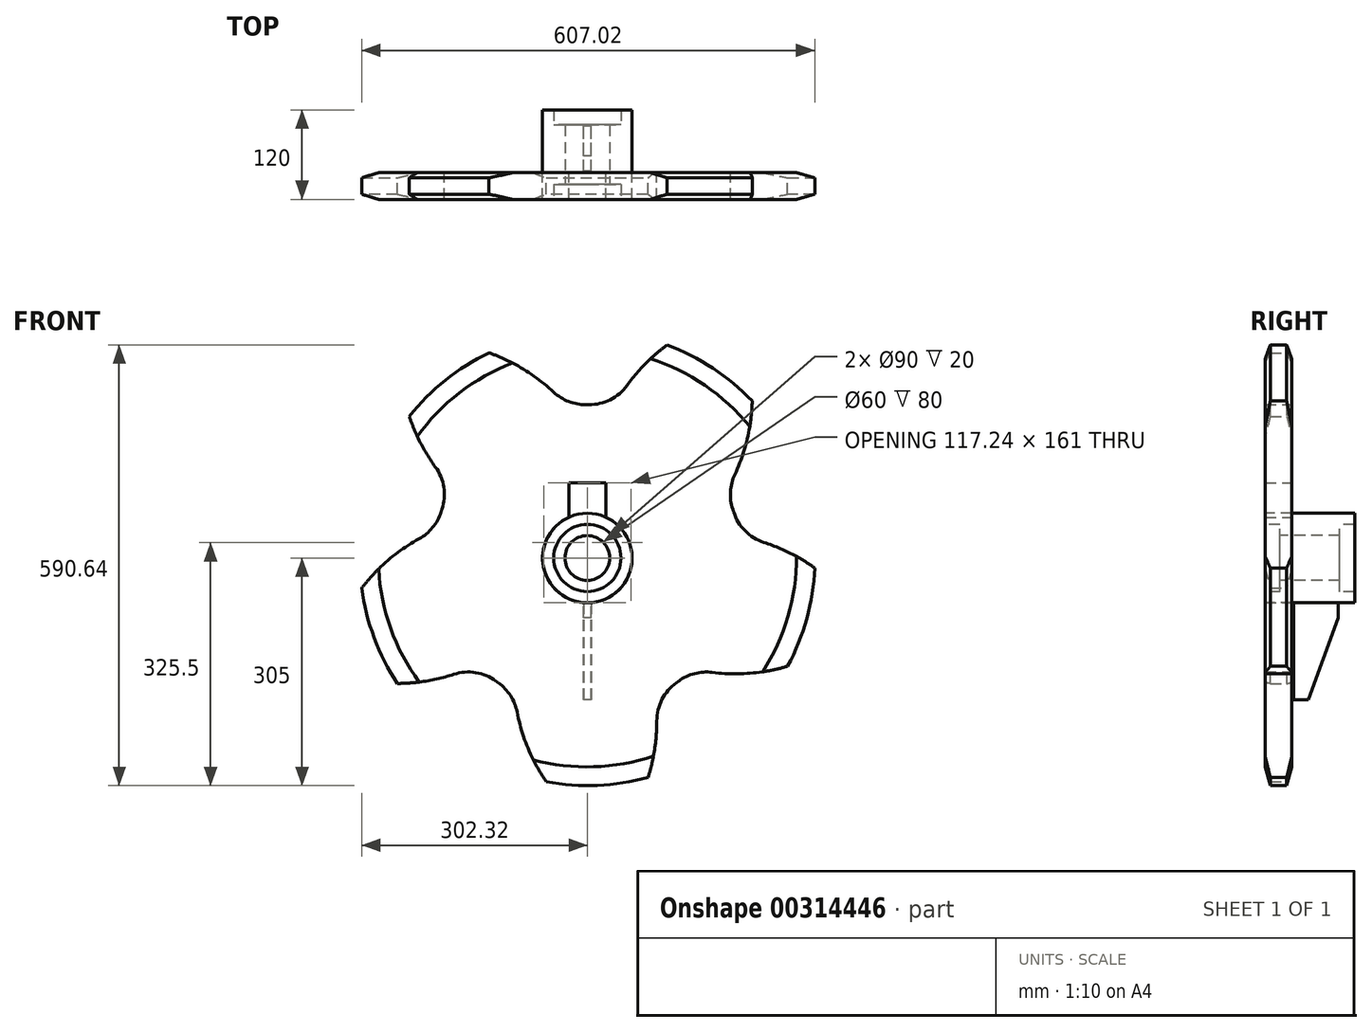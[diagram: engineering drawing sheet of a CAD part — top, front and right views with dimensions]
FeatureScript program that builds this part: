
annotation { "Feature Type Name" : "Feature", "Feature Type Description" : "" }
export const myFeature = defineFeature(function(context is Context, id is Id, definition is map)
    precondition{}
    {
        {
            var Q0;
            Q0=qCreatedBy(makeId("Front.planeOp"),FACE);
            var sketch = newSketch(context, id + "F0", { "sketchPlane" : qUnion([Q0])});
            skArc(sketch, "E0.0", {"start": v(-131.78, 275.06) * mm, "mid": v(-190.02, 238.57) * mm, "end": v(-238.6, 189.98) * mm});
            skLineSegment(sketch, "E1", {"start": v(-25, 54.54) * mm, "end": v(-25, 101) * mm});
            skLineSegment(sketch, "E2", {"start": v(-25, 101) * mm, "end": v(25, 101) * mm});
            skLineSegment(sketch, "E3", {"start": v(25, 101) * mm, "end": v(25, 54.54) * mm});
            skLineSegment(sketch, "E4", {"start": v(0, 0) * mm, "end": v(0, 397.7) * mm, "construction": true});
            skArc(sketch, "E5", {"start": v(25, 54.54) * mm, "mid": v(0, 60) * mm, "end": v(-25, 54.54) * mm, "construction": true});
            skArc(sketch, "E6", {"start": v(-25, 54.54) * mm, "mid": v(0, -60) * mm, "end": v(25, 54.54) * mm});
            skCircle(sketch, "E7", {"center": v(0, 0) * mm, "radius": 268 * mm, "construction": true});
            skCircle(sketch, "E8", {"center": v(0, 0) * mm, "radius": 218.5 * mm, "construction": true});
            skLineSegment(sketch, "E9", {"start": v(2.5, 288.37) * mm, "end": v(2.5, 267.99) * mm, "construction": true});
            skLineSegment(sketch, "E10.MirrorCS", {"start": v(-2.5, 288.37) * mm, "end": v(-2.5, 267.99) * mm, "construction": true});
            skLineSegment(sketch, "E11", {"start": v(2.5, 267.99) * mm, "end": v(2.5, 234) * mm, "construction": true});
            skLineSegment(sketch, "E12", {"start": v(-2.5, 267.99) * mm, "end": v(-2.5, 234) * mm, "construction": true});
            skArc(sketch, "E13", {"start": v(-45.24, 222.38) * mm, "mid": v(-24.3, 209.42) * mm, "end": v(0, 205.54) * mm});
            skCircle(sketch, "E14", {"center": v(0, 0) * mm, "radius": 205.5 * mm});
            skArc(sketch, "E15", {"start": v(-45.24, 222.38) * mm, "mid": v(-85.78, 253.2) * mm, "end": v(-131.78, 275.06) * mm});
            skArc(sketch, "E16", {"start": v(106.94, 285.64) * mm, "mid": v(77.94, 260.6) * mm, "end": v(53.15, 231.37) * mm});
            skArc(sketch, "E17.trimOffspring", {"start": v(0, 205.54) * mm, "mid": v(29.82, 211.78) * mm, "end": v(53.15, 231.37) * mm});
            skPoint(sketch, "E18.center", {"position": v(0.01, 0.07) * mm});
            skArc(sketch, "E19.1.0", {"start": v(-225.48, 25.7) * mm, "mid": v(-206.68, 41.6) * mm, "end": v(-195.48, 63.51) * mm});
            skArc(sketch, "E19.1.1", {"start": v(-225.48, 25.7) * mm, "mid": v(-267.31, -3.34) * mm, "end": v(-302.32, -40.33) * mm});
            skLineSegment(sketch, "E19.1.2", {"start": v(-273.48, 91.49) * mm, "end": v(-254.1, 85.2) * mm, "construction": true});
            skLineSegment(sketch, "E19.1.3", {"start": v(-275.02, 86.73) * mm, "end": v(-255.64, 80.44) * mm, "construction": true});
            skLineSegment(sketch, "E19.1.4", {"start": v(-254.1, 85.2) * mm, "end": v(-221.78, 74.69) * mm, "construction": true});
            skLineSegment(sketch, "E19.1.5", {"start": v(-255.64, 80.44) * mm, "end": v(-223.32, 69.93) * mm, "construction": true});
            skArc(sketch, "E19.1.6", {"start": v(-238.6, 189.98) * mm, "mid": v(-223.75, 154.65) * mm, "end": v(-203.62, 122.04) * mm});
            skArc(sketch, "E19.1.7", {"start": v(-195.48, 63.51) * mm, "mid": v(-192.2, 93.8) * mm, "end": v(-203.62, 122.04) * mm});
            skArc(sketch, "E19.2.0", {"start": v(-94.12, -206.5) * mm, "mid": v(-103.43, -183.71) * mm, "end": v(-120.81, -166.28) * mm});
            skArc(sketch, "E19.2.1", {"start": v(-94.12, -206.5) * mm, "mid": v(-79.42, -255.26) * mm, "end": v(-55.06, -299.99) * mm});
            skLineSegment(sketch, "E19.2.2", {"start": v(-171.52, -231.82) * mm, "end": v(-159.54, -215.34) * mm, "construction": true});
            skLineSegment(sketch, "E19.2.3", {"start": v(-167.47, -234.76) * mm, "end": v(-155.5, -218.28) * mm, "construction": true});
            skLineSegment(sketch, "E19.2.4", {"start": v(-159.54, -215.34) * mm, "end": v(-139.57, -187.84) * mm, "construction": true});
            skLineSegment(sketch, "E19.2.5", {"start": v(-155.5, -218.28) * mm, "end": v(-135.52, -190.78) * mm, "construction": true});
            skArc(sketch, "E19.2.6", {"start": v(-254.41, -168.22) * mm, "mid": v(-216.22, -165.01) * mm, "end": v(-179, -155.94) * mm});
            skArc(sketch, "E19.2.7", {"start": v(-120.81, -166.28) * mm, "mid": v(-148.6, -153.8) * mm, "end": v(-179, -155.94) * mm});
            skArc(sketch, "E19.3.0", {"start": v(167.3, -153.32) * mm, "mid": v(142.76, -155.13) * mm, "end": v(120.81, -166.28) * mm});
            skArc(sketch, "E19.3.1", {"start": v(167.3, -153.32) * mm, "mid": v(218.23, -154.42) * mm, "end": v(268.3, -145.07) * mm});
            skLineSegment(sketch, "E19.3.2", {"start": v(167.47, -234.76) * mm, "end": v(155.5, -218.28) * mm, "construction": true});
            skLineSegment(sketch, "E19.3.3", {"start": v(171.52, -231.82) * mm, "end": v(159.54, -215.34) * mm, "construction": true});
            skLineSegment(sketch, "E19.3.4", {"start": v(155.5, -218.28) * mm, "end": v(135.52, -190.78) * mm, "construction": true});
            skLineSegment(sketch, "E19.3.5", {"start": v(159.54, -215.34) * mm, "end": v(139.57, -187.84) * mm, "construction": true});
            skArc(sketch, "E19.3.6", {"start": v(81.37, -293.94) * mm, "mid": v(90.12, -256.63) * mm, "end": v(93, -218.42) * mm});
            skArc(sketch, "E19.3.7", {"start": v(120.81, -166.28) * mm, "mid": v(100.35, -188.86) * mm, "end": v(93, -218.42) * mm});
            skArc(sketch, "E19.4.0", {"start": v(197.52, 111.74) * mm, "mid": v(191.66, 87.83) * mm, "end": v(195.48, 63.51) * mm});
            skArc(sketch, "E19.4.1", {"start": v(197.52, 111.74) * mm, "mid": v(214.3, 159.83) * mm, "end": v(220.88, 210.33) * mm});
            skLineSegment(sketch, "E19.4.2", {"start": v(275.02, 86.73) * mm, "end": v(255.64, 80.44) * mm, "construction": true});
            skLineSegment(sketch, "E19.4.3", {"start": v(273.48, 91.49) * mm, "end": v(254.1, 85.2) * mm, "construction": true});
            skLineSegment(sketch, "E19.4.4", {"start": v(255.64, 80.44) * mm, "end": v(223.32, 69.93) * mm, "construction": true});
            skLineSegment(sketch, "E19.4.5", {"start": v(254.1, 85.2) * mm, "end": v(221.78, 74.69) * mm, "construction": true});
            skArc(sketch, "E19.4.6", {"start": v(304.7, -13.44) * mm, "mid": v(271.92, 6.4) * mm, "end": v(236.47, 20.95) * mm});
            skArc(sketch, "E19.4.7", {"start": v(195.48, 63.51) * mm, "mid": v(210.62, 37.08) * mm, "end": v(236.47, 20.95) * mm});
            skArc(sketch, "E20.trimOffspring", {"start": v(220.88, 210.33) * mm, "mid": v(168.18, 254.44) * mm, "end": v(106.94, 285.64) * mm});
            skArc(sketch, "E21.trimOffspring", {"start": v(-302.32, -40.33) * mm, "mid": v(-285.62, -107) * mm, "end": v(-254.41, -168.22) * mm});
            skArc(sketch, "E22.trimOffspring", {"start": v(-55.06, -299.99) * mm, "mid": v(13.5, -304.7) * mm, "end": v(81.37, -293.94) * mm});
            skArc(sketch, "E23.trimOffspring", {"start": v(268.3, -145.07) * mm, "mid": v(293.96, -81.32) * mm, "end": v(304.7, -13.44) * mm});
            skSolve(sketch);
        }
        {
            var Q0;
            Q0=makeQuery(id+"F0.imprint","IMPRINT",FACE,{"disambiguationData":[TD([[makeQuery(id+"F0.imprint","IMPRINT",EDGE,{"derivedFrom":sQuery(id+"F0.wireOp",EDGE,"E0.0")}),1.0]])]});
            var Q1;
            Q1=makeQuery(id+"F0.imprint","IMPRINT",FACE,{"disambiguationData":[TD([[makeQuery(id+"F0.imprint","IMPRINT",EDGE,{"derivedFrom":sQuery(id+"F0.wireOp",EDGE,"E1")}),1.0]])]});
            var Q2;
            {var subQ5=sQuery(id+"F0.wireOp",EDGE,"E16");Q2=makeQuery(id+"F0.imprint","IMPRINT",FACE,{"disambiguationData":[TD([[makeQuery(id+"F0.imprint","IMPRINT",EDGE,{"derivedFrom":subQ5}),1.0]])]});}
            var Q3;
            {var subQ1=sQuery(id+"F0.wireOp",EDGE,"E19.3.1");Q3=makeQuery(id+"F0.imprint","IMPRINT",FACE,{"disambiguationData":[TD([[makeQuery(id+"F0.imprint","IMPRINT",EDGE,{"derivedFrom":subQ1}),1.0]])]});}
            var Q4;
            {var subQ6=sQuery(id+"F0.wireOp",EDGE,"E19.2.1");Q4=makeQuery(id+"F0.imprint","IMPRINT",FACE,{"disambiguationData":[TD([[makeQuery(id+"F0.imprint","IMPRINT",EDGE,{"derivedFrom":subQ6}),1.0]])]});}
            var Q5;
            {var subQ1=sQuery(id+"F0.wireOp",EDGE,"E19.1.1");Q5=makeQuery(id+"F0.imprint","IMPRINT",FACE,{"disambiguationData":[TD([[makeQuery(id+"F0.imprint","IMPRINT",EDGE,{"derivedFrom":subQ1}),1.0]])]});}
            extrude(context, id + "F1", {"entities" : qUnion([Q0, Q1, Q2, Q3, Q4, Q5]), "depth" : 36 * mm, "offsetDistance" : 25 * mm, "symmetric" : true});
        }
        {
            var Q0;
            Q0=qCreatedBy(makeId("Right.planeOp"),FACE);
            var sketch = newSketch(context, id + "F2", { "sketchPlane" : qUnion([Q0])});
            skPoint(sketch, "E24.0", {"position": v(-18, -304.7) * mm});
            skLineSegment(sketch, "E25", {"start": v(0, 0) * mm, "end": v(0, -348.46) * mm, "construction": true});
            skLineSegment(sketch, "E26", {"start": v(-18, -304.7) * mm, "end": v(-11, -304.7) * mm});
            skLineSegment(sketch, "E27", {"start": v(-11, -304.7) * mm, "end": v(-18, -280) * mm});
            skLineSegment(sketch, "E28", {"start": v(-18, -280) * mm, "end": v(-18, -304.7) * mm});
            skLineSegment(sketch, "E29.MirrorCS", {"start": v(11, -304.7) * mm, "end": v(18, -280) * mm});
            skLineSegment(sketch, "E30.MirrorCS", {"start": v(18, -280) * mm, "end": v(18, -304.7) * mm});
            skLineSegment(sketch, "E31.MirrorCS", {"start": v(18, -304.7) * mm, "end": v(11, -304.7) * mm});
            skLineSegment(sketch, "E32", {"start": v(-18, -304.7) * mm, "end": v(-18, -324.2) * mm});
            skLineSegment(sketch, "E33", {"start": v(-18, -324.2) * mm, "end": v(-5.47, -324.2) * mm});
            skLineSegment(sketch, "E34", {"start": v(-5.47, -324.2) * mm, "end": v(-11, -304.7) * mm});
            skLineSegment(sketch, "E35", {"start": v(18, -304.7) * mm, "end": v(18, -323.36) * mm});
            skLineSegment(sketch, "E36", {"start": v(18, -323.36) * mm, "end": v(5.71, -323.36) * mm});
            skLineSegment(sketch, "E37", {"start": v(5.71, -323.36) * mm, "end": v(11, -304.7) * mm});
            skSolve(sketch);
        }
        {
            var Q0;
            Q0=qCreatedBy(makeId("Right.planeOp"),FACE);
            var sketch = newSketch(context, id + "F3", { "sketchPlane" : qUnion([Q0])});
            skLineSegment(sketch, "E38", {"start": v(0, 0) * mm, "end": v(129.22, 0) * mm, "construction": true});
            skSolve(sketch);
        }
        {
            var Q0;
            Q0 = qSketchRegion(id + "F2", true);
            var Q1;
            Q1=sQuery(id+"F3.wireOp",EDGE,"E38");
            revolve(context, id + "F4", {"operationType" : NewBodyOperationType.REMOVE, "entities" : qUnion([Q0]), "axis" : qUnion([Q1]), "revolveType" : RevolveType.FULL, "oppositeDirection" : true});
        }
        {
            var Q0;
            Q0=qCreatedBy(makeId("Right.planeOp"),FACE);
            var sketch = newSketch(context, id + "F5", { "sketchPlane" : qUnion([Q0])});
            skLineSegment(sketch, "E39.0", {"start": v(-18, 54.54) * mm, "end": v(-18, -60) * mm});
            skLineSegment(sketch, "E40", {"start": v(0, 0) * mm, "end": v(110.3, 0) * mm, "construction": true});
            skLineSegment(sketch, "E41", {"start": v(-18, -60) * mm, "end": v(102, -60) * mm});
            skLineSegment(sketch, "E42", {"start": v(102, -60) * mm, "end": v(102, -45) * mm});
            skLineSegment(sketch, "E43", {"start": v(102, -45) * mm, "end": v(82, -45) * mm});
            skLineSegment(sketch, "E44", {"start": v(82, -45) * mm, "end": v(82, -30) * mm});
            skLineSegment(sketch, "E45", {"start": v(82, -30) * mm, "end": v(2, -30) * mm});
            skLineSegment(sketch, "E46", {"start": v(2, -30) * mm, "end": v(2, -45) * mm});
            skLineSegment(sketch, "E47", {"start": v(2, -45) * mm, "end": v(-18, -45) * mm});
            skLineSegment(sketch, "E48", {"start": v(20, -60) * mm, "end": v(20, -190) * mm});
            skLineSegment(sketch, "E49", {"start": v(20, -190) * mm, "end": v(40, -190) * mm});
            skLineSegment(sketch, "E50", {"start": v(40, -190) * mm, "end": v(80, -80) * mm});
            skLineSegment(sketch, "E51", {"start": v(80, -80) * mm, "end": v(80, -60) * mm});
            skSolve(sketch);
        }
        {
            var Q0;
            {var subQ0=sQuery(id+"F5.wireOp",EDGE,"E41");Q0=makeQuery(id+"F5.imprint","IMPRINT",FACE,{"disambiguationData":[TD([[makeQuery(id+"F5.imprint","IMPRINT",EDGE,{"derivedFrom":subQ0}),1.0]])]});}
            var Q1;
            Q1=sQuery(id+"F5.wireOp",EDGE,"E40");
            revolve(context, id + "F6", {"entities" : qUnion([Q0]), "axis" : qUnion([Q1]), "revolveType" : RevolveType.FULL});
        }
        {
            var Q0;
            {var subQ0=sQuery(id+"F5.wireOp",EDGE,"E48");Q0=makeQuery(id+"F5.imprint","IMPRINT",FACE,{"disambiguationData":[TD([[makeQuery(id+"F5.imprint","IMPRINT",EDGE,{"derivedFrom":subQ0}),1.0]])]});}
            extrude(context, id + "F7", {"entities" : qUnion([Q0]), "depth" : 10 * mm, "offsetDistance" : 25 * mm, "symmetric" : true});
        }
    });
